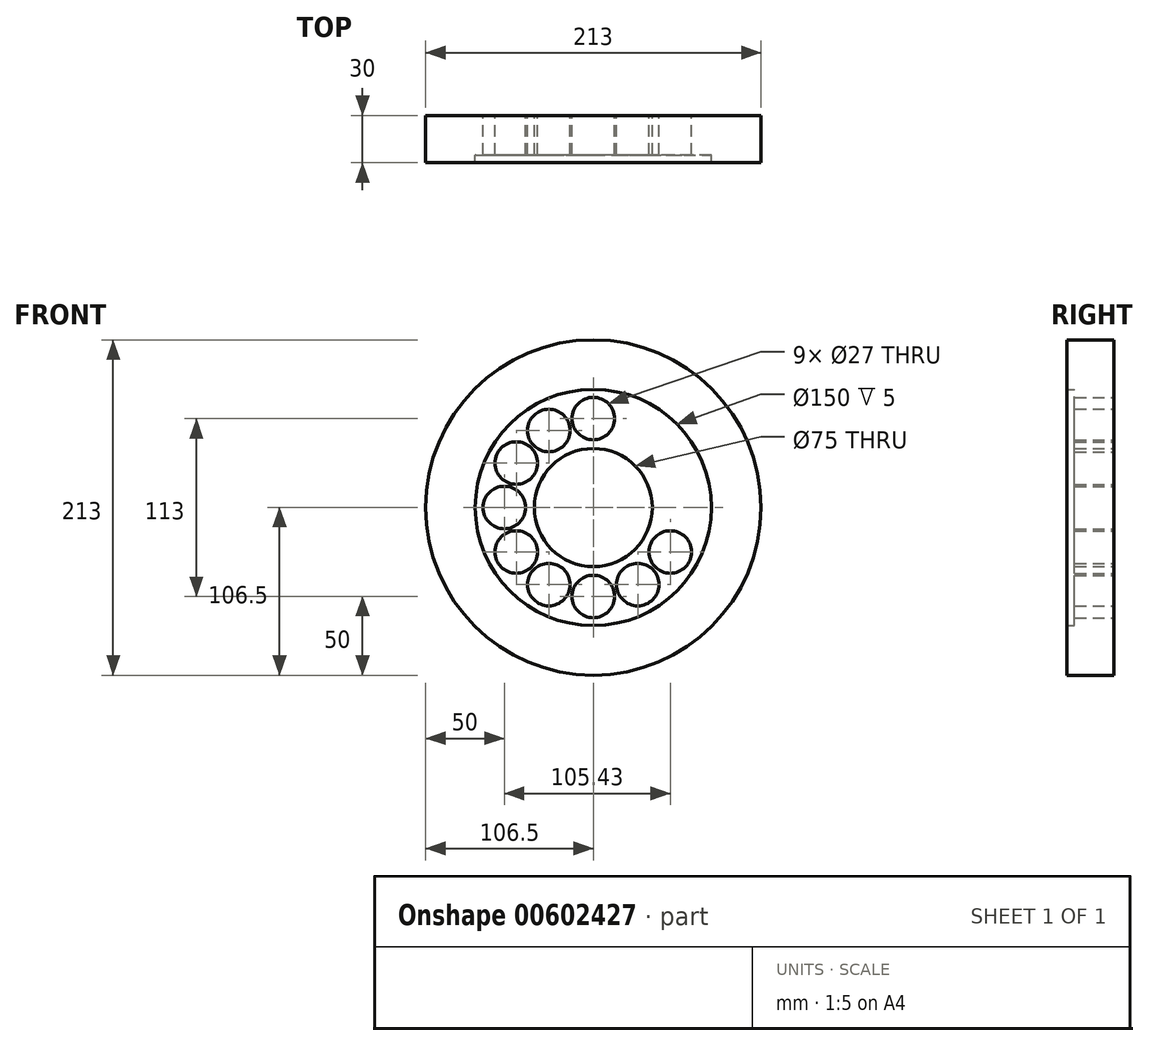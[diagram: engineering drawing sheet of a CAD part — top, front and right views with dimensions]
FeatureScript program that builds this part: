
annotation { "Feature Type Name" : "Feature", "Feature Type Description" : "" }
export const myFeature = defineFeature(function(context is Context, id is Id, definition is map)
    precondition{}
    {
        {
            var Q0;
            Q0=qCreatedBy(makeId("Front.planeOp"),FACE);
            var sketch = newSketch(context, id + "F0", { "sketchPlane" : qUnion([Q0])});
            skCircle(sketch, "E0", {"center": v(0, 0) * mm, "radius": 32.5 * mm});
            skCircle(sketch, "E1", {"center": v(0, 0) * mm, "radius": 37.5 * mm});
            skCircle(sketch, "E2", {"center": v(0, 0) * mm, "radius": 56.5 * mm, "construction": true});
            skCircle(sketch, "E3", {"center": v(0, 0) * mm, "radius": 75 * mm});
            skCircle(sketch, "E4", {"center": v(0, 0) * mm, "radius": 106.5 * mm});
            skCircle(sketch, "E5", {"center": v(0, 56.5) * mm, "radius": 13.5 * mm});
            skCircle(sketch, "E6", {"center": v(-56.5, 0) * mm, "radius": 13.5 * mm});
            skCircle(sketch, "E7", {"center": v(-48.93, 28.25) * mm, "radius": 13.5 * mm});
            skCircle(sketch, "E8", {"center": v(-28.25, 48.93) * mm, "radius": 13.5 * mm});
            skCircle(sketch, "E9", {"center": v(0, -56.5) * mm, "radius": 13.5 * mm});
            skCircle(sketch, "E10", {"center": v(-28.25, -48.93) * mm, "radius": 13.5 * mm});
            skCircle(sketch, "E11", {"center": v(-48.93, -28.25) * mm, "radius": 13.5 * mm});
            skCircle(sketch, "E12", {"center": v(28.25, -48.93) * mm, "radius": 13.5 * mm});
            skCircle(sketch, "E13", {"center": v(48.93, -28.25) * mm, "radius": 13.5 * mm});
            skLineSegment(sketch, "E14", {"start": v(0, 56.5) * mm, "end": v(0, 0) * mm});
            skLineSegment(sketch, "E15", {"start": v(-28.25, 48.93) * mm, "end": v(0, 0) * mm});
            skLineSegment(sketch, "E16", {"start": v(-48.93, 28.25) * mm, "end": v(0, 0) * mm});
            skLineSegment(sketch, "E17", {"start": v(-56.5, 0) * mm, "end": v(0, 0) * mm});
            skLineSegment(sketch, "E18", {"start": v(-48.93, -28.25) * mm, "end": v(0, 0) * mm});
            skLineSegment(sketch, "E19", {"start": v(-28.25, -48.93) * mm, "end": v(0, 0) * mm});
            skLineSegment(sketch, "E20", {"start": v(0, -56.5) * mm, "end": v(0, 0) * mm});
            skLineSegment(sketch, "E21", {"start": v(28.25, -48.93) * mm, "end": v(0, 0) * mm});
            skLineSegment(sketch, "E22", {"start": v(48.93, -28.25) * mm, "end": v(0, 0) * mm});
            skSolve(sketch);
        }
        {
            var Q0;
            Q0=makeQuery(id+"F0.imprint","IMPRINT",FACE,{"disambiguationData":[TD([[makeQuery(id+"F0.imprint","IMPRINT",EDGE,{"derivedFrom":sQuery(id+"F0.wireOp",EDGE,"E3")}),-1.0]])]});
            extrude(context, id + "F1", {"entities" : qUnion([Q0]), "depth" : 30 * mm, "offsetDistance" : 25 * mm});
        }
        {
            var Q0;
            Q0=makeQuery(id+"F0.imprint","IMPRINT",FACE,{"disambiguationData":[TD([[makeQuery(id+"F0.imprint","IMPRINT",EDGE,{"derivedFrom":sQuery(id+"F0.wireOp",EDGE,"E3")}),1.0]])]});
            extrude(context, id + "F2", {"entities" : qUnion([Q0]), "operationType" : NewBodyOperationType.ADD, "depth" : 25 * mm, "offsetDistance" : 25 * mm});
        }
    });
